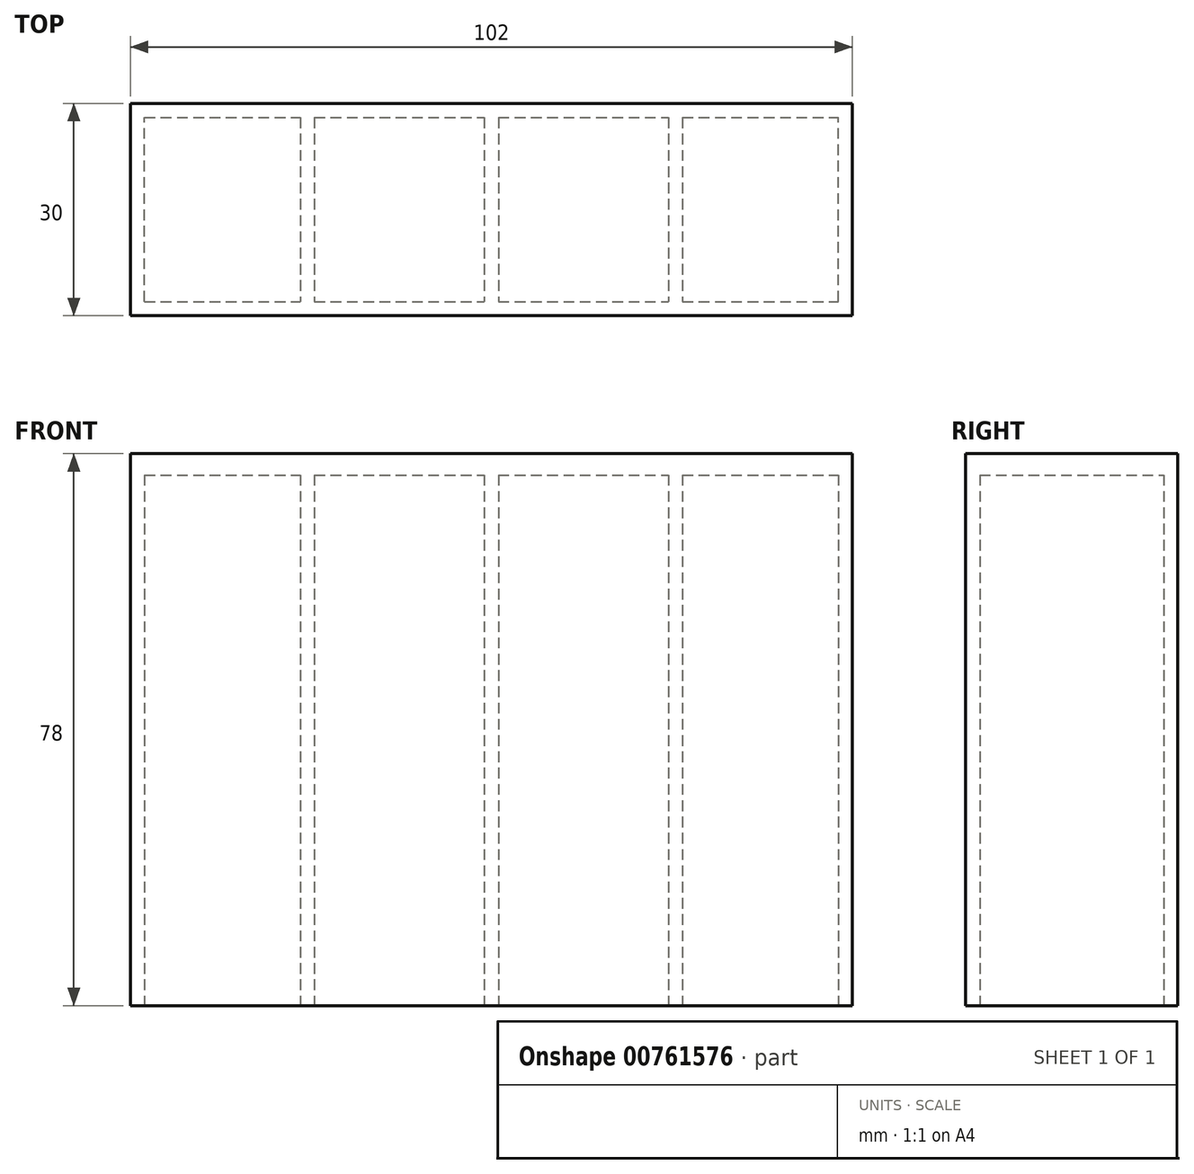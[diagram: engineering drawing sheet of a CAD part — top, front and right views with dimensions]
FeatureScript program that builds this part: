
annotation { "Feature Type Name" : "Feature", "Feature Type Description" : "" }
export const myFeature = defineFeature(function(context is Context, id is Id, definition is map)
    precondition{}
    {
        {
            var Q0;
            Q0=qCreatedBy(makeId("Top.planeOp"),FACE);
            var sketch = newSketch(context, id + "F0", { "sketchPlane" : qUnion([Q0])});
            skLineSegment(sketch, "E0.bottom", {"start": v(2, 0) * mm, "end": v(24, 0) * mm});
            skLineSegment(sketch, "E0.top", {"start": v(2, 26) * mm, "end": v(24, 26) * mm});
            skLineSegment(sketch, "E0.left", {"start": v(0, -2) * mm, "end": v(0, 28) * mm});
            skLineSegment(sketch, "E0.right", {"start": v(100, 0) * mm, "end": v(100, 26) * mm});
            skLineSegment(sketch, "E1", {"start": v(26, 26) * mm, "end": v(26, 0) * mm});
            skLineSegment(sketch, "E2", {"start": v(50, 26) * mm, "end": v(50, 0) * mm});
            skLineSegment(sketch, "E3", {"start": v(76, 26) * mm, "end": v(76, 0) * mm});
            skLineSegment(sketch, "E4.0", {"start": v(2, 0) * mm, "end": v(2, 26) * mm});
            skLineSegment(sketch, "E5.0", {"start": v(102, -2) * mm, "end": v(102, 28) * mm});
            skLineSegment(sketch, "E6.0", {"start": v(24, 26) * mm, "end": v(24, 0) * mm});
            skLineSegment(sketch, "E7.0", {"start": v(52, 26) * mm, "end": v(52, 0) * mm});
            skLineSegment(sketch, "E8.0", {"start": v(78, 26) * mm, "end": v(78, 0) * mm});
            skLineSegment(sketch, "E9.trimOffspring", {"start": v(26, 26) * mm, "end": v(50, 26) * mm});
            skLineSegment(sketch, "E10.trimOffspring", {"start": v(26, 0) * mm, "end": v(50, 0) * mm});
            skLineSegment(sketch, "E11.trimOffspring", {"start": v(52, 26) * mm, "end": v(76, 26) * mm});
            skLineSegment(sketch, "E12.trimOffspring", {"start": v(52, 0) * mm, "end": v(76, 0) * mm});
            skLineSegment(sketch, "E13.trimOffspring", {"start": v(78, 0) * mm, "end": v(100, 0) * mm});
            skLineSegment(sketch, "E14.trimOffspring", {"start": v(78, 26) * mm, "end": v(100, 26) * mm});
            skPoint(sketch, "E15.orphan", {"position": v(0, 0) * mm});
            skPoint(sketch, "E16.orphan", {"position": v(0, 26) * mm});
            skLineSegment(sketch, "E17", {"start": v(0, -2) * mm, "end": v(102, -2) * mm});
            skLineSegment(sketch, "E18", {"start": v(102, 28) * mm, "end": v(0, 28) * mm});
            skSolve(sketch);
        }
        {
            var Q0;
            Q0=makeQuery(id+"F0.imprint","IMPRINT",FACE,{"disambiguationData":[TD([[makeQuery(id+"F0.imprint","IMPRINT",EDGE,{"derivedFrom":sQuery(id+"F0.wireOp",EDGE,"E0.bottom")}),-1.0]])]});
            extrude(context, id + "F1", {"entities" : qUnion([Q0]), "depth" : 75 * mm, "offsetDistance" : 25 * mm});
        }
        {
            var Q0;
            Q0=makeQuery(id+"F1.opExtrude","CAP_FACE",FACE,{"disambiguationData":[OSD([sQuery(id+"F0.wireOp",EDGE,"E0.bottom"),sQuery(id+"F0.wireOp",EDGE,"E0.top"),sQuery(id+"F0.wireOp",EDGE,"E0.left"),sQuery(id+"F0.wireOp",EDGE,"E0.right"),sQuery(id+"F0.wireOp",EDGE,"E1"),sQuery(id+"F0.wireOp",EDGE,"E2"),sQuery(id+"F0.wireOp",EDGE,"E3"),sQuery(id+"F0.wireOp",EDGE,"E4.0"),sQuery(id+"F0.wireOp",EDGE,"E5.0"),sQuery(id+"F0.wireOp",EDGE,"E6.0"),sQuery(id+"F0.wireOp",EDGE,"E7.0"),sQuery(id+"F0.wireOp",EDGE,"E8.0"),sQuery(id+"F0.wireOp",EDGE,"E9.trimOffspring"),sQuery(id+"F0.wireOp",EDGE,"E10.trimOffspring"),sQuery(id+"F0.wireOp",EDGE,"E11.trimOffspring"),sQuery(id+"F0.wireOp",EDGE,"E12.trimOffspring"),sQuery(id+"F0.wireOp",EDGE,"E13.trimOffspring"),sQuery(id+"F0.wireOp",EDGE,"E14.trimOffspring"),sQuery(id+"F0.wireOp",EDGE,"E17"),sQuery(id+"F0.wireOp",EDGE,"E18")])],"isStart":false});
            var sketch = newSketch(context, id + "F2", { "sketchPlane" : qUnion([Q0])});
            skLineSegment(sketch, "E19.bottom", {"start": v(0, -2) * mm, "end": v(102, -2) * mm});
            skLineSegment(sketch, "E19.top", {"start": v(0, 28) * mm, "end": v(102, 28) * mm});
            skLineSegment(sketch, "E19.left", {"start": v(0, -2) * mm, "end": v(0, 28) * mm});
            skLineSegment(sketch, "E19.right", {"start": v(102, -2) * mm, "end": v(102, 28) * mm});
            skSolve(sketch);
        }
        {
            var Q0;
            Q0 = qSketchRegion(id + "F2", true);
            extrude(context, id + "F3", {"entities" : qUnion([Q0]), "operationType" : NewBodyOperationType.ADD, "depth" : 3 * mm, "offsetDistance" : 25 * mm});
        }
    });
